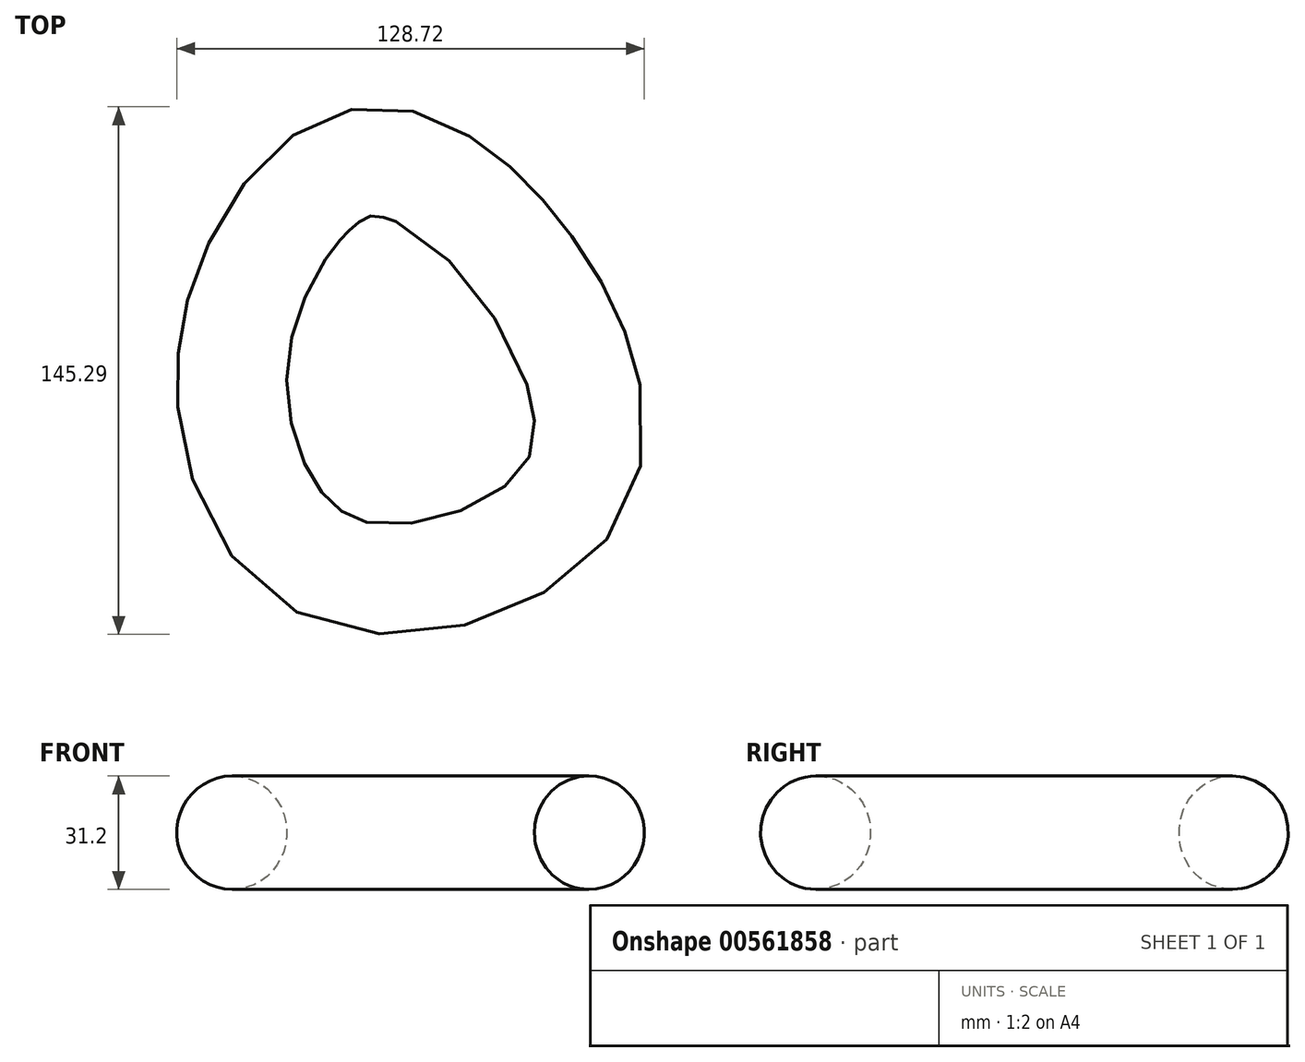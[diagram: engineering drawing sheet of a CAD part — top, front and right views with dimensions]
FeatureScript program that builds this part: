
annotation { "Feature Type Name" : "Feature", "Feature Type Description" : "" }
export const myFeature = defineFeature(function(context is Context, id is Id, definition is map)
    precondition{}
    {
        {
            var Q0;
            Q0=qCreatedBy(makeId("Top.planeOp"),FACE);
            var sketch = newSketch(context, id + "F0", { "sketchPlane" : qUnion([Q0])});
            skFitSpline(sketch, "E0", {"points": [v(-23.63, 59.61) * mm, v(21.95, 23.16) * mm, v(27.54, -30.88) * mm, v(-31.8, -50.18) * mm, v(-60.6, -11.58) * mm, v(-53.3, 34.3) * mm, v(-23.63, 59.61) * mm]});
            skSolve(sketch);
        }
        {
            var Q0;
            Q0=qCreatedBy(makeId("Front.planeOp"),FACE);
            var sketch = newSketch(context, id + "F1", { "sketchPlane" : qUnion([Q0])});
            skCircle(sketch, "E1", {"center": v(33.48, 0) * mm, "radius": 15.6 * mm});
            skSolve(sketch);
        }
        {
            var Q0;
            Q0=makeQuery(id+"F1.imprint","IMPRINT",FACE,{"disambiguationData":[TD([[makeQuery(id+"F1.imprint","IMPRINT",EDGE,{"derivedFrom":sQuery(id+"F1.wireOp",EDGE,"E1")}),1.0]])]});
            var Q1;
            Q1=sQuery(id+"F0.wireOp",EDGE,"E0");
            sweep(context, id + "F2", {"profiles" : qUnion([Q0]), "path" : qUnion([Q1])});
        }
    });
